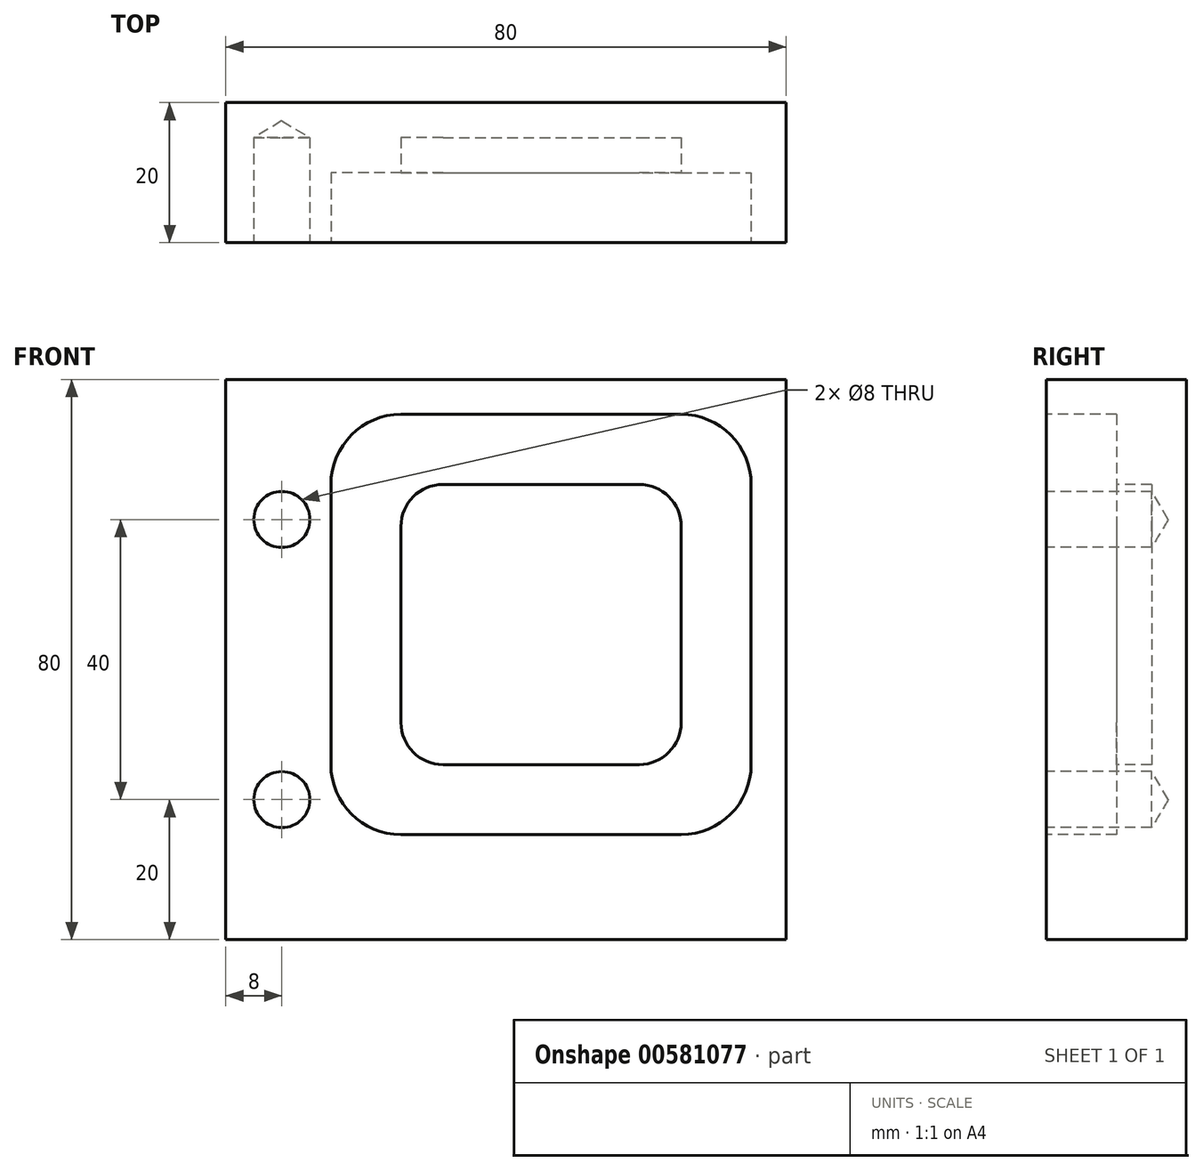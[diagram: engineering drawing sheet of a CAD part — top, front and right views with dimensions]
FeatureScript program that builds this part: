
annotation { "Feature Type Name" : "Feature", "Feature Type Description" : "" }
export const myFeature = defineFeature(function(context is Context, id is Id, definition is map)
    precondition{}
    {
        {
            var Q0;
            Q0=qCreatedBy(makeId("Front.planeOp"),FACE);
            var sketch = newSketch(context, id + "F0", { "sketchPlane" : qUnion([Q0])});
            skLineSegment(sketch, "E0.bottom", {"start": v(-40, -40) * mm, "end": v(40, -40) * mm});
            skLineSegment(sketch, "E0.top", {"start": v(-40, 40) * mm, "end": v(40, 40) * mm});
            skLineSegment(sketch, "E0.left", {"start": v(-40, -40) * mm, "end": v(-40, 40) * mm});
            skLineSegment(sketch, "E0.right", {"start": v(40, -40) * mm, "end": v(40, 40) * mm});
            skPoint(sketch, "E0.middle", {"position": v(0, 0) * mm});
            skSolve(sketch);
        }
        {
            var Q0;
            Q0=makeQuery(id+"F0.imprint","IMPRINT",FACE,{"disambiguationData":[TD([[makeQuery(id+"F0.imprint","IMPRINT",EDGE,{"derivedFrom":sQuery(id+"F0.wireOp",EDGE,"E0.bottom")}),1.0]])]});
            extrude(context, id + "F1", {"entities" : qUnion([Q0]), "depth" : 20 * mm, "offsetDistance" : 25 * mm});
        }
        {
            var Q0;
            Q0=makeQuery(id+"F1.opExtrude","CAP_FACE",FACE,{"disambiguationData":[OSD([sQuery(id+"F0.wireOp",EDGE,"E0.bottom"),sQuery(id+"F0.wireOp",EDGE,"E0.top"),sQuery(id+"F0.wireOp",EDGE,"E0.left"),sQuery(id+"F0.wireOp",EDGE,"E0.right"),sQuery(id+"F0.wireOp",EDGE,"iOFf9txA-A6VU-KnUf-DTI9-ZGf5BK90oHoW"),sQuery(id+"F0.wireOp",EDGE,"G50O9v60-QSTp-3VJk-jash-wJoZvsjcVbLV")])],"isStart":false});
            var sketch = newSketch(context, id + "F2", { "sketchPlane" : qUnion([Q0])});
            skCircle(sketch, "E1", {"center": v(-32, 20) * mm, "radius": 4 * mm});
            skCircle(sketch, "E2", {"center": v(-32, -20) * mm, "radius": 4 * mm});
            skSolve(sketch);
        }
        {
            var Q0;
            Q0=sQuery(id+"F2.wireOp",VERTEX,"E1.center");
            var Q1;
            Q1=sQuery(id+"F2.wireOp",VERTEX,"E2.center");
            var Q2;
            Q2=makeQuery(id+"F1.opExtrude","SWEPT_BODY",BODY,{"disambiguationData":[OSD([sQuery(id+"F0.wireOp",EDGE,"E0.bottom"),sQuery(id+"F0.wireOp",EDGE,"E0.top"),sQuery(id+"F0.wireOp",EDGE,"E0.left"),sQuery(id+"F0.wireOp",EDGE,"E0.right")])]});
            hole(context, id + "F3", {"style" : HoleStyle.SIMPLE, "endStyle" : HoleEndStyle.BLIND, "holeDiameter" : 8 * mm, "majorDiameter" : 5 * mm, "holeDepth" : 15 * mm, "isTappedThrough" : true, "tappedDepth" : 12 * mm, "tapClearance" : 3, "locations" : qUnion([Q0, Q1]), "scope" : qUnion([Q2])});
        }
        {
            var Q0;
            Q0=makeQuery(id+"F1.opExtrude","CAP_FACE",FACE,{"disambiguationData":[OSD([sQuery(id+"F0.wireOp",EDGE,"E0.bottom"),sQuery(id+"F0.wireOp",EDGE,"E0.top"),sQuery(id+"F0.wireOp",EDGE,"E0.left"),sQuery(id+"F0.wireOp",EDGE,"E0.right")])],"isStart":false});
            var sketch = newSketch(context, id + "F4", { "sketchPlane" : qUnion([Q0])});
            skLineSegment(sketch, "E3.bottom", {"start": v(-15, 35) * mm, "end": v(25, 35) * mm});
            skLineSegment(sketch, "E3.top", {"start": v(-15, -25) * mm, "end": v(25, -25) * mm});
            skLineSegment(sketch, "E3.left", {"start": v(-25, 25) * mm, "end": v(-25, -15) * mm});
            skLineSegment(sketch, "E3.right", {"start": v(35, 25) * mm, "end": v(35, -15) * mm});
            skPoint(sketch, "E4.visualSharp", {"position": v(35, 35) * mm});
            skArc(sketch, "E4.filletArc", {"start": v(35, 25) * mm, "mid": v(32.07, 32.07) * mm, "end": v(25, 35) * mm});
            skPoint(sketch, "E5.visualSharp", {"position": v(-25, 35) * mm});
            skArc(sketch, "E5.filletArc", {"start": v(-15, 35) * mm, "mid": v(-22.07, 32.07) * mm, "end": v(-25, 25) * mm});
            skPoint(sketch, "E6.visualSharp", {"position": v(-25, -25) * mm});
            skArc(sketch, "E6.filletArc", {"start": v(-25, -15) * mm, "mid": v(-22.07, -22.07) * mm, "end": v(-15, -25) * mm});
            skPoint(sketch, "E7.visualSharp", {"position": v(35, -25) * mm});
            skArc(sketch, "E7.filletArc", {"start": v(25, -25) * mm, "mid": v(32.07, -22.07) * mm, "end": v(35, -15) * mm});
            skLineSegment(sketch, "E8.bottom", {"start": v(-9, 25) * mm, "end": v(19, 25) * mm});
            skLineSegment(sketch, "E8.top", {"start": v(-9, -15) * mm, "end": v(19, -15) * mm});
            skLineSegment(sketch, "E8.left", {"start": v(-15, 19) * mm, "end": v(-15, -9) * mm});
            skLineSegment(sketch, "E8.right", {"start": v(25, 19) * mm, "end": v(25, -9) * mm});
            skArc(sketch, "E9.filletArc", {"start": v(-9, 25) * mm, "mid": v(-13.24, 23.24) * mm, "end": v(-15, 19) * mm});
            skArc(sketch, "E10.filletArc", {"start": v(-15, -9) * mm, "mid": v(-13.24, -13.24) * mm, "end": v(-9, -15) * mm});
            skArc(sketch, "E11.filletArc", {"start": v(25, 19) * mm, "mid": v(23.24, 23.24) * mm, "end": v(19, 25) * mm});
            skArc(sketch, "E12.filletArc", {"start": v(19, -15) * mm, "mid": v(23.24, -13.24) * mm, "end": v(25, -9) * mm});
            skSolve(sketch);
        }
        {
            var Q0;
            Q0=makeQuery(id+"F4.imprint","IMPRINT",FACE,{"disambiguationData":[TD([[makeQuery(id+"F4.imprint","IMPRINT",EDGE,{"derivedFrom":sQuery(id+"F4.wireOp",EDGE,"E3.bottom")}),-1.0]])]});
            extrude(context, id + "F5", {"entities" : qUnion([Q0]), "operationType" : NewBodyOperationType.REMOVE, "oppositeDirection" : true, "depth" : 10 * mm, "offsetDistance" : 25 * mm});
        }
        {
            var Q0;
            Q0=makeQuery(id+"F5.boolean.opBoolean","SPLIT",FACE,{"disambiguationData":[TD([makeQuery(id+"F5.opExtrude","SWEPT_FACE",FACE,{"disambiguationData":[OSD([sQuery(id+"F4.wireOp",EDGE,"E8.bottom")])]})])],"derivedFrom":makeQuery(id+"F1.opExtrude","CAP_FACE",FACE,{"disambiguationData":[OSD([sQuery(id+"F0.wireOp",EDGE,"E0.bottom"),sQuery(id+"F0.wireOp",EDGE,"E0.top"),sQuery(id+"F0.wireOp",EDGE,"E0.left"),sQuery(id+"F0.wireOp",EDGE,"E0.right")])],"isStart":false})});
            extrude(context, id + "F6", {"entities" : qUnion([Q0]), "operationType" : NewBodyOperationType.REMOVE, "oppositeDirection" : true, "depth" : 15 * mm, "offsetDistance" : 25 * mm});
        }
    });
